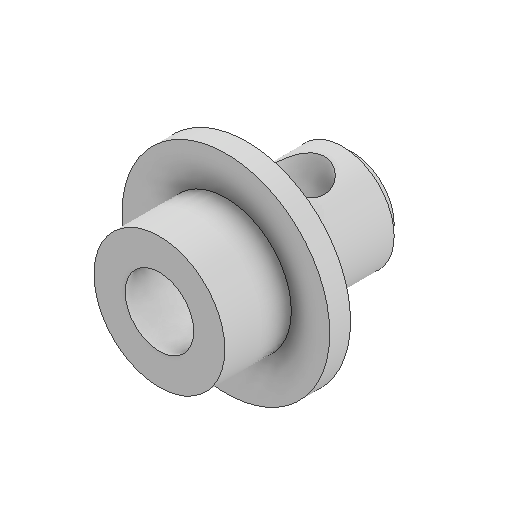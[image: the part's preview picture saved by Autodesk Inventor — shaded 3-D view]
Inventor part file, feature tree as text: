
AUTODESK INVENTOR PART (.ipt)
format: ipt  version: 2022 (Build 260153000, 153)  size: 124,416 bytes
history: native  units: in
note: dims shown in document units (in); Inventor stores cm internally (conversion verified against a paired STEP export)
features: chamfer x1
ambient origin geometry x8: Origin, YZ Plane, XZ Plane, XY Plane, X Axis, Y Axis, Z Axis, Center Point
bodies: Solid1 (feature_tree)
feature tree (1):
  chamfer  "Chamfer1"  [1 undecoded]
note: 1 required parameter value undecoded (feature->parameter linkage not recoverable at this tier; creation-order binding heuristic only, values carry confidence <= 0.55)
